# Revit family: Drinking_Fountain-Haws_Corporation-Pedestal_3380
name_source: partatom
category: Plumbing Fixtures
revit_build: Autodesk Revit Architecture 2013 (Build: 20130531_2115(x64)
units: mm (PartAtom-declared; Revit-internal decimal feet)

## types (4) — shared parameters
Assembly Code = D2010810
Bowl = Metal - Haws Corporation - High Polished Stainless Steel
Bowl Height = 27"
Cost = $0.00
Cost Note = For Cost information please visit the Resource tab in the Product Page URL
Flow = 0.00 GPM
Full Length = 40 1/2"
Keynote = 15410.A1
Manufacturer = Haws Corporation 1455 Kleppe Lane Sparks, NV 89431
Product Documentation Link = http://www.hawsco.com
Product Page URL = http://www.hawsco.com
Sanitary Radius = 1"
Series = Haws heavy-duty pedestal drinking fountains
Supply Radius = 1/2"
To Spot Outlet = 36"
URL = http://www.hawsco.com

## per-type parameters (varying)
| type | CWFU | Description | HW Connection | HWFU | Pedestal | Type Comments | Vent Connection | WFU | Waste Connection |
| 3380 | 1 | Without freeze-resistant valve assembly | No | 1 | Metal - Haws Corporation - Green Powder Coated Finish | Heavy-duty 11 gauge fabricated galvanized steel with green powder-coated finish | No | 1 | Yes |
| 3380FR | 2 | Use a freeze-resistant valve assembly to provide year round operation | No | 2 | Metal - Haws Corporation - Green Powder Coated Finish | Heavy-duty 11 gauge thick steel with green powder-coated finish | Yes | 2 | No |
| 3380G | 3 | 3380G allows the circular pedestal to be placed securely in multiple locations | Yes | 3 | Metal - Haws Corporation - Galvanized Steel | Heavy-duty 11 gauge thick steel with galvanized finish | No | 3 | Yes |
| 3380GFR | 3 | Uses a freeze-resistant valve assembly | Yes | 3 | Metal - Haws Corporation - Galvanized Steel | Heavy-duty 11 gauge thick steel with galvanized finish | No | 3 | Yes |

note: column(s) folded — value = type name in every type: Model

## geometry (parser evidence)
native form markers: Blend x23, Sweep x5
no freeform markers — native parametric forms only
